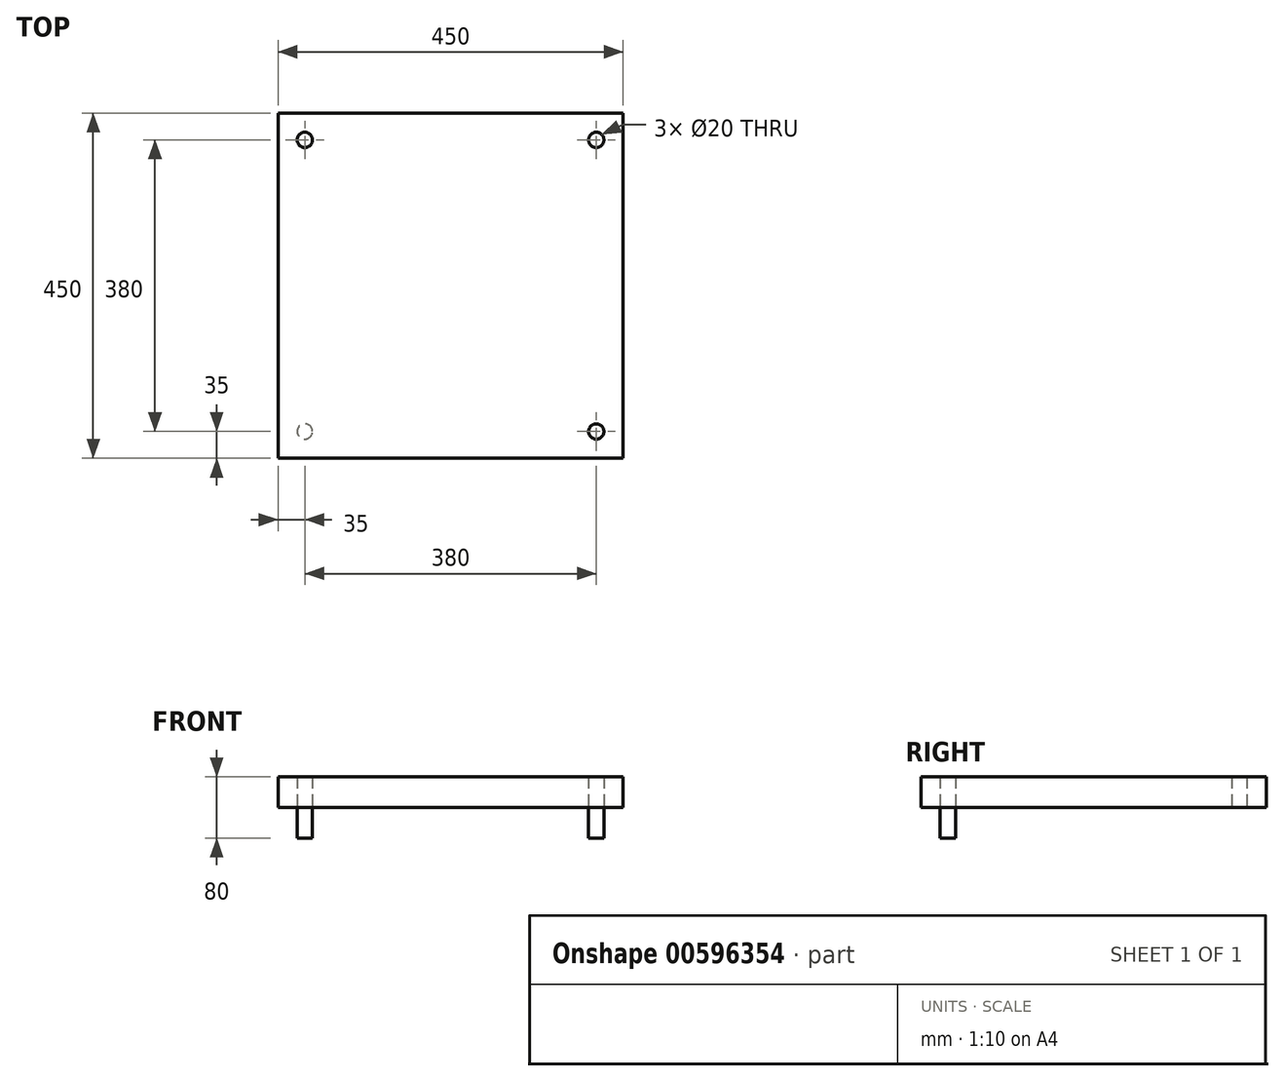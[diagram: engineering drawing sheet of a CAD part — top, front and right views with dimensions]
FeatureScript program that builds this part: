
annotation { "Feature Type Name" : "Feature", "Feature Type Description" : "" }
export const myFeature = defineFeature(function(context is Context, id is Id, definition is map)
    precondition{}
    {
        {
            var Q0;
            Q0=qCreatedBy(makeId("Top.planeOp"),FACE);
            var sketch = newSketch(context, id + "F0", { "sketchPlane" : qUnion([Q0])});
            skLineSegment(sketch, "E0.bottom", {"start": v(225, -225) * mm, "end": v(-225, -225) * mm});
            skLineSegment(sketch, "E0.top", {"start": v(225, 225) * mm, "end": v(-225, 225) * mm});
            skLineSegment(sketch, "E0.left", {"start": v(225, -225) * mm, "end": v(225, 225) * mm});
            skLineSegment(sketch, "E0.right", {"start": v(-225, -225) * mm, "end": v(-225, 225) * mm});
            skPoint(sketch, "E0.middle", {"position": v(0, 0) * mm});
            skSolve(sketch);
        }
        {
            var Q0;
            Q0=makeQuery(id+"F0.imprint","IMPRINT",FACE,{"disambiguationData":[TD([[makeQuery(id+"F0.imprint","IMPRINT",EDGE,{"derivedFrom":sQuery(id+"F0.wireOp",EDGE,"E0.bottom")}),-1.0]])]});
            var sketch = newSketch(context, id + "F1", { "sketchPlane" : qUnion([Q0])});
            skCircle(sketch, "E1", {"center": v(-190, 190) * mm, "radius": 10 * mm});
            skCircle(sketch, "E2", {"center": v(190, 190) * mm, "radius": 10 * mm});
            skCircle(sketch, "E3", {"center": v(-190, -190) * mm, "radius": 10 * mm});
            skCircle(sketch, "E4", {"center": v(190, -190) * mm, "radius": 10 * mm});
            skSolve(sketch);
        }
        {
            var Q0;
            Q0=makeQuery(id+"F1.imprint","IMPRINT",FACE,{"disambiguationData":[TD([[makeQuery(id+"F1.imprint","IMPRINT",EDGE,{"derivedFrom":sQuery(id+"F1.wireOp",EDGE,"E1")}),-1.0]])]});
            extrude(context, id + "F2", {"entities" : qUnion([Q0]), "depth" : 40 * mm, "offsetDistance" : 25 * mm});
        }
        {
            var Q0;
            Q0=makeQuery(id+"F2.opExtrude","CAP_FACE",FACE,{"disambiguationData":[OSD([sQuery(id+"F0.wireOp",EDGE,"E0.bottom"),sQuery(id+"F0.wireOp",EDGE,"E0.top"),sQuery(id+"F0.wireOp",EDGE,"E0.left"),sQuery(id+"F0.wireOp",EDGE,"E0.right"),sQuery(id+"F1.wireOp",EDGE,"E1"),sQuery(id+"F1.wireOp",EDGE,"E2"),sQuery(id+"F1.wireOp",EDGE,"E3"),sQuery(id+"F1.wireOp",EDGE,"E4")])],"isStart":false});
            var sketch = newSketch(context, id + "F3", { "sketchPlane" : qUnion([Q0])});
            skCircle(sketch, "E5.0", {"center": v(190, -190) * mm, "radius": 10 * mm});
            skCircle(sketch, "E6.0", {"center": v(-190, -190) * mm, "radius": 10 * mm});
            skCircle(sketch, "E6.1", {"center": v(-190, 190) * mm, "radius": 10 * mm});
            skCircle(sketch, "E6.2", {"center": v(190, 190) * mm, "radius": 10 * mm});
            skSolve(sketch);
        }
        {
            var Q0;
            Q0=makeQuery(id+"F3.imprint","IMPRINT",FACE,{"disambiguationData":[TD([[makeQuery(id+"F3.imprint","IMPRINT",EDGE,{"derivedFrom":sQuery(id+"F3.wireOp",EDGE,"E6.0")}),1.0]])]});
            extrude(context, id + "F4", {"entities" : qUnion([Q0]), "operationType" : NewBodyOperationType.ADD, "oppositeDirection" : true, "depth" : 80 * mm, "offsetDistance" : 25 * mm});
        }
        {
            var Q0;
            Q0=makeQuery(id+"F3.imprint","IMPRINT",FACE,{"disambiguationData":[TD([[makeQuery(id+"F3.imprint","IMPRINT",EDGE,{"derivedFrom":sQuery(id+"F3.wireOp",EDGE,"E5.0")}),1.0]])]});
            var Q1;
            Q1=sQuery(id+"F3.wireOp",EDGE,"E5.0");
            extrude(context, id + "F5", {"entities" : qUnion([Q0]), "surfaceEntities" : qUnion([Q1]), "oppositeDirection" : true, "depth" : 80 * mm, "offsetDistance" : 25 * mm});
        }
    });
